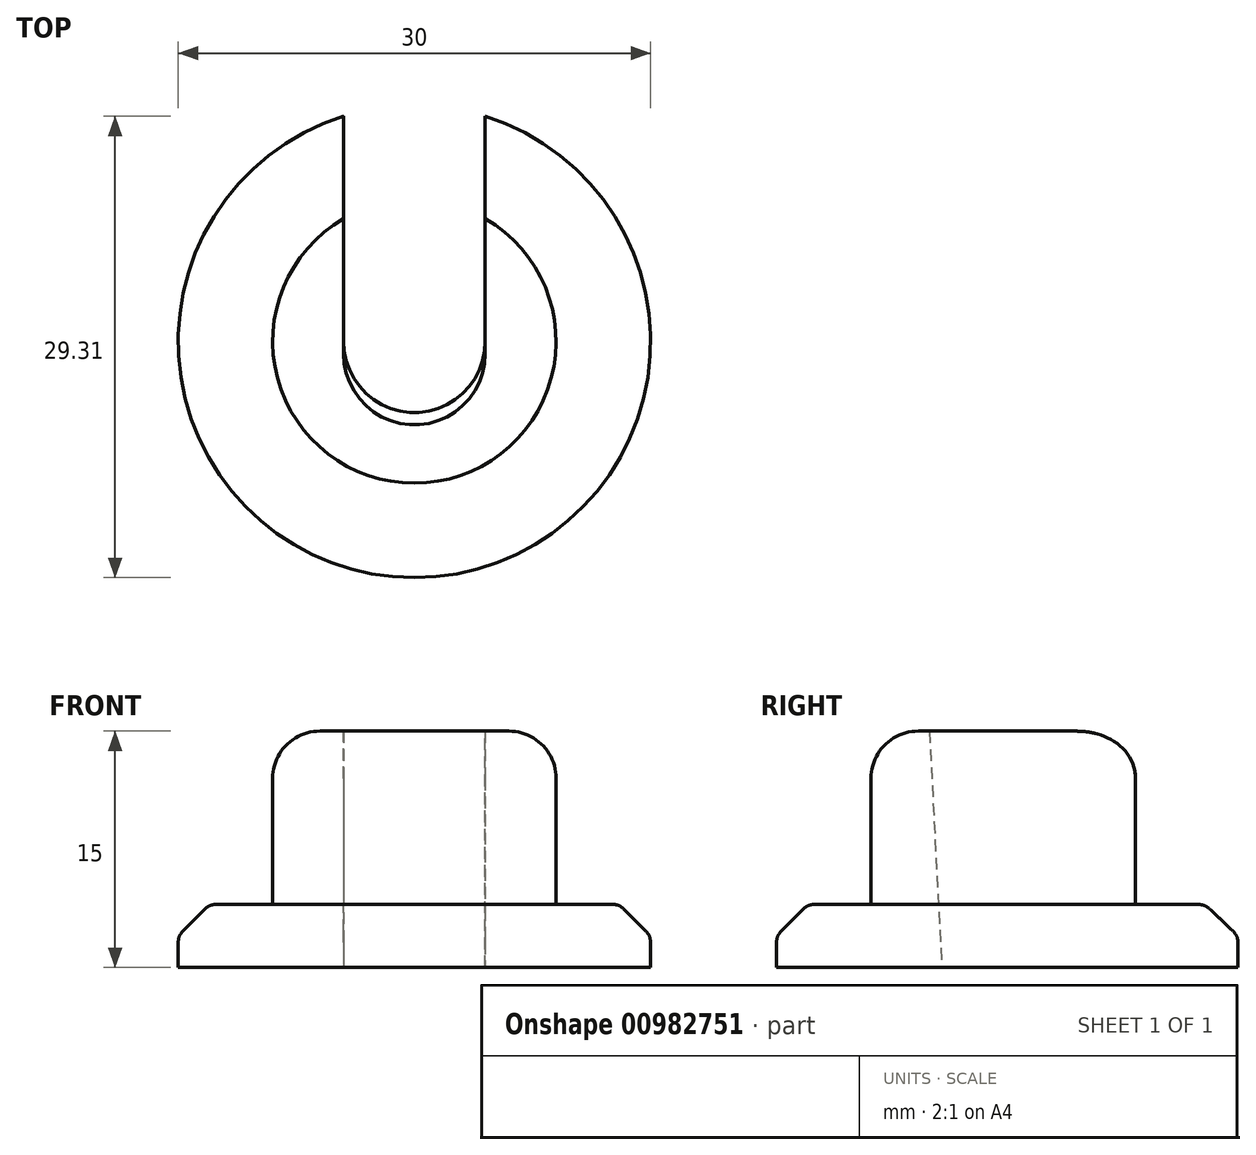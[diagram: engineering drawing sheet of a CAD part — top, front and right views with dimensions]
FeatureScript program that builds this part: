
annotation { "Feature Type Name" : "Feature", "Feature Type Description" : "" }
export const myFeature = defineFeature(function(context is Context, id is Id, definition is map)
    precondition{}
    {
        {
            var Q0;
            Q0=qCreatedBy(makeId("Top.planeOp"),FACE);
            var sketch = newSketch(context, id + "F0", { "sketchPlane" : qUnion([Q0])});
            skCircle(sketch, "E0", {"center": v(0, 0) * mm, "radius": 15 * mm});
            skCircle(sketch, "E1", {"center": v(0, 0) * mm, "radius": 9 * mm});
            skLineSegment(sketch, "E2", {"start": v(-15, 0) * mm, "end": v(15, 0) * mm, "construction": true});
            skSolve(sketch);
        }
        {
            var Q0;
            Q0=makeQuery(id+"F0.imprint","IMPRINT",FACE,{"disambiguationData":[TD([[makeQuery(id+"F0.imprint","IMPRINT",EDGE,{"derivedFrom":sQuery(id+"F0.wireOp",EDGE,"E0")}),1.0]])]});
            extrude(context, id + "F1", {"entities" : qUnion([Q0]), "depth" : 4 * mm, "offsetDistance" : 25 * mm});
        }
        {
            var Q0;
            Q0=makeQuery(id+"F0.imprint","IMPRINT",FACE,{"disambiguationData":[TD([[makeQuery(id+"F0.imprint","IMPRINT",EDGE,{"derivedFrom":sQuery(id+"F0.wireOp",EDGE,"E1")}),1.0]])]});
            extrude(context, id + "F2", {"entities" : qUnion([Q0]), "operationType" : NewBodyOperationType.ADD, "depth" : 15 * mm, "offsetDistance" : 25 * mm});
        }
        {
            var Q0;
            Q0=sQuery(id+"F0.wireOp",EDGE,"E2");
            cPlane(context, id + "F3", {"entities" : qUnion([Q0]), "cplaneType" : CPlaneType.LINE_ANGLE, "offset" : 25 * mm, "angle" : 93 * degree, "width" : 150 * mm, "height" : 150 * mm});
        }
        {
            var Q0;
            Q0=qCreatedBy(id+"F3.planeOp",FACE);
            var sketch = newSketch(context, id + "F4", { "sketchPlane" : qUnion([Q0])});
            skCircle(sketch, "E3", {"center": v(0, 0) * mm, "radius": 4.5 * mm});
            skSolve(sketch);
        }
        {
            var Q0;
            Q0=makeQuery(id+"F4.imprint","IMPRINT",FACE,{"disambiguationData":[TD([[makeQuery(id+"F4.imprint","IMPRINT",EDGE,{"derivedFrom":sQuery(id+"F4.wireOp",EDGE,"E3")}),1.0]])]});
            extrude(context, id + "F5", {"entities" : qUnion([Q0]), "operationType" : NewBodyOperationType.REMOVE, "endBound" : BoundingType.SYMMETRIC, "depth" : 47.4 * mm, "offsetDistance" : 25 * mm});
        }
        {
            var Q0;
            Q0=sQuery(id+"F0.wireOp",EDGE,"E2");
            cPlane(context, id + "F6", {"entities" : qUnion([Q0]), "cplaneType" : CPlaneType.LINE_ANGLE, "offset" : 25 * mm, "angle" : 3 * degree, "width" : 150 * mm, "height" : 150 * mm});
        }
        {
            var Q0;
            Q0=qCreatedBy(id+"F6.planeOp",FACE);
            var sketch = newSketch(context, id + "F7", { "sketchPlane" : qUnion([Q0])});
            skLineSegment(sketch, "E4", {"start": v(-4.5, -2.82) * mm, "end": v(-4.5, 15.02) * mm});
            skLineSegment(sketch, "E5", {"start": v(4.5, 15.02) * mm, "end": v(4.5, -2.67) * mm});
            skLineSegment(sketch, "E6", {"start": v(5.85, -2.65) * mm, "end": v(-6.32, -2.85) * mm, "construction": true});
            skLineSegment(sketch, "E7", {"start": v(4.5, 15.02) * mm, "end": v(-4.5, 15.02) * mm});
            skLineSegment(sketch, "E8", {"start": v(4.5, -2.67) * mm, "end": v(-4.5, -2.82) * mm});
            skSolve(sketch);
        }
        {
            var Q0;
            Q0=qSketchRegion(id+"F7",true);
            extrude(context, id + "F8", {"entities" : qUnion([Q0]), "operationType" : NewBodyOperationType.REMOVE, "depth" : 25 * mm, "offsetDistance" : 25 * mm});
        }
        {
            var Q0;
            Q0=makeQuery(id+"F1.opExtrude","CAP_EDGE",EDGE,{"disambiguationData":[OSD([sQuery(id+"F0.wireOp",EDGE,"E0")])],"isStart":false});
            chamfer(context, id + "F9", {"entities" : qUnion([Q0]), "width" : 2 * mm, "tangentPropagation" : true});
        }
        {
            var Q0;
            Q0=makeQuery(id+"F1.opExtrude","CAP_EDGE",EDGE,{"disambiguationData":[OSD([sQuery(id+"F0.wireOp",EDGE,"E1")])],"isStart":false});
            var Q1;
            Q1=makeQuery(id+"F2.opExtrude","CAP_EDGE",EDGE,{"disambiguationData":[OSD([sQuery(id+"F0.wireOp",EDGE,"E1")])],"isStart":false});
            fillet(context, id + "F10", {"entities" : qUnion([Q0, Q1]), "radius" : 3 * mm, "tangentPropagation" : true, "allowEdgeOverflow" : false});
        }
        {
            var Q0;
            Q0=makeQuery(id+"F10.opFillet","BLEND_EDGE",EDGE,{"blendedFrom":[makeQuery(id+"F1.opExtrude","CAP_EDGE",EDGE,{"disambiguationData":[OSD([sQuery(id+"F0.wireOp",EDGE,"E1")])],"isStart":false}),makeQuery(id+"F8.boolean.opBoolean","COPY",FACE,{"derivedFrom":makeQuery(id+"F8.opExtrude","SWEPT_FACE",FACE,{"disambiguationData":[OSD([sQuery(id+"F7.wireOp",EDGE,"E5")])]})})],"blendedInto":[makeQuery(id+"F8.boolean.opBoolean","COPY",FACE,{"derivedFrom":makeQuery(id+"F8.opExtrude","SWEPT_FACE",FACE,{"disambiguationData":[OSD([sQuery(id+"F7.wireOp",EDGE,"E5")])]})})]});
            var Q1;
            {var subQ0=sQuery(id+"F0.wireOp",EDGE,"E0");Q1=makeQuery(id+"F9.opChamfer","BLEND_EDGE",EDGE,{"blendedFrom":[makeQuery(id+"F1.opExtrude","CAP_EDGE",EDGE,{"disambiguationData":[OSD([subQ0])],"isStart":false}),makeQuery(id+"F1.opExtrude","CAP_FACE",FACE,{"disambiguationData":[OSD([subQ0,sQuery(id+"F0.wireOp",EDGE,"E1")])],"isStart":false})],"blendedInto":[makeQuery(id+"F1.opExtrude","CAP_FACE",FACE,{"disambiguationData":[OSD([subQ0,sQuery(id+"F0.wireOp",EDGE,"E1")])],"isStart":false})]});}
            var Q2;
            {var subQ0=sQuery(id+"F0.wireOp",EDGE,"E0");Q2=makeQuery(id+"F9.opChamfer","BLEND_EDGE",EDGE,{"blendedFrom":[makeQuery(id+"F1.opExtrude","CAP_EDGE",EDGE,{"disambiguationData":[OSD([subQ0])],"isStart":false}),makeQuery(id+"F1.opExtrude","SWEPT_FACE",FACE,{"disambiguationData":[OSD([subQ0])]})],"blendedInto":[makeQuery(id+"F1.opExtrude","SWEPT_FACE",FACE,{"disambiguationData":[OSD([subQ0])]})]});}
            fillet(context, id + "F11", {"entities" : qUnion([Q0, Q1, Q2]), "radius" : 1 * mm, "tangentPropagation" : true, "allowEdgeOverflow" : false});
        }
    });
